# Revit family: VSY12
name_source: partatom
category: Lighting Fixtures
units: mm (PartAtom-declared; Revit-internal decimal feet)

## family parameters
Cut with Voids When Loaded = No
Host = Face
Light Source = Yes
OmniClass Number = 23.80.70.11
OmniClass Title = Luminaries for Internal Lighting
Part Type = Normal
Room Calculation Point = No
Round Connector Dimension = Use Diameter
Shared = No

## types (1)
- VSY12
    Apparent Load = 0 VA
    Backbox = White
    Certification = IC label is standard for recessed products
• All luminaires are built to UL1598 and
2108 standards, and bear appropriate
cCSAus labels
• Damp Location label standard. Emergencyequipped fixtures labeled UL 924
• Adheres to LM79, LM80, and TM21
industry standards
    Color Filter = 16777215
    Default Elevation = 48"
    Description = VERSIFY™ 1'X2' ARCHITECTURAL EDGE-LIT
    Dimming Lamp Color Temperature Shift = <None>
    Emit Shape Visible in Rendering = No
    Emit from Rectangle Length = 24"
    Emit from Rectangle Width = 12"
    Features = Architectural styling in an edge-lit luminaire
• High efficiency acrylic lens featuring edge lit technology
• Ideal for offices, schools, medical, and public spaces
• Up to 140 lumens per watt
• Stylish controls integration
• 2inch overall depth, 2 1/4inch with emergency battery pack
• Certified UL924 for fixtures with battery or DTS (Dimming Bypass
Module) options
    Frame = Paint - Gray Smooth
    Lamp = LED lamp
    Light Bulb = White Glass
    Load Classification = Lighting
    Manufacturer = Columbia Lighting
    Model = VSY12
    Photometric Web File = VSY12-30HLHE-EDU.ies
    Row Length = 24"
    Tilt Angle = -90.00°
    URL = https://www.currentlighting.com
    Voltage = 120 V
    Warranty = Five-year warranty
    Wattage Comments = 11-33W
    Width = 12"
    zz Length = 23"

## geometry (parser evidence)
native form markers: Sweep x1
no freeform markers — native parametric forms only
